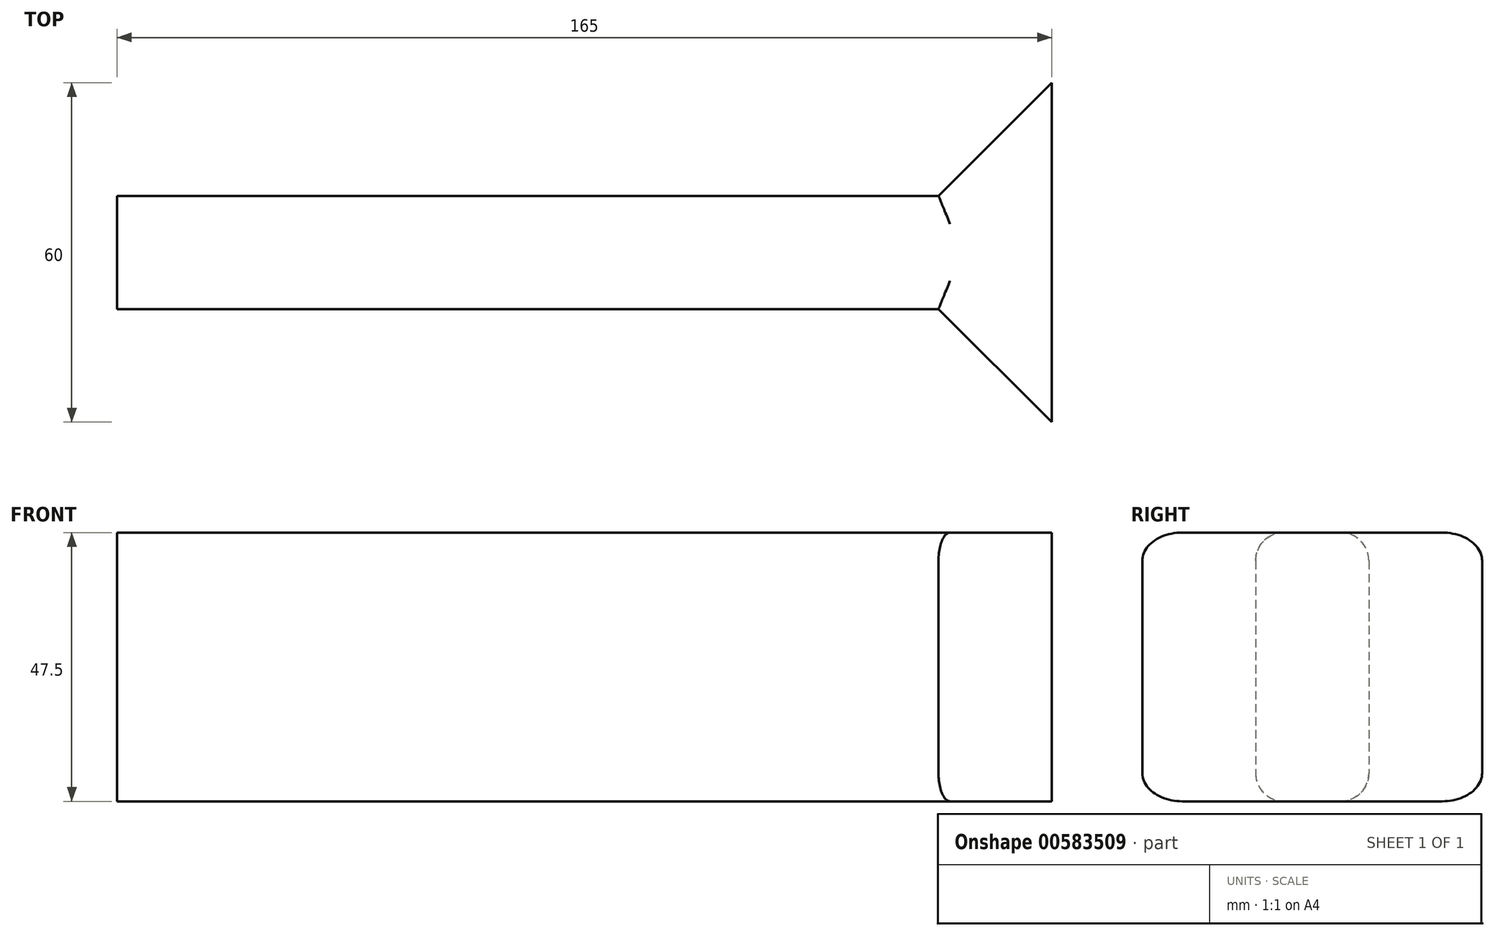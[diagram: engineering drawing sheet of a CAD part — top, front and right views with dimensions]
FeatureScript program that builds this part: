
annotation { "Feature Type Name" : "Feature", "Feature Type Description" : "" }
export const myFeature = defineFeature(function(context is Context, id is Id, definition is map)
    precondition{}
    {
        {
            var Q0;
            Q0=qCreatedBy(makeId("Top.planeOp"),FACE);
            var sketch = newSketch(context, id + "F0", { "sketchPlane" : qUnion([Q0])});
            skLineSegment(sketch, "E0.bottom", {"start": v(-165, -20) * mm, "end": v(-20, -20) * mm});
            skLineSegment(sketch, "E0.top", {"start": v(-165, 0) * mm, "end": v(-20, 0) * mm});
            skLineSegment(sketch, "E0.left", {"start": v(-165, -20) * mm, "end": v(-165, 0) * mm});
            skLineSegment(sketch, "E0.right", {"start": v(0, -20) * mm, "end": v(0, 0) * mm});
            skLineSegment(sketch, "E1.left", {"start": v(0, 0) * mm, "end": v(0, 20) * mm});
            skLineSegment(sketch, "E2", {"start": v(0, -20) * mm, "end": v(0, -40) * mm});
            skLineSegment(sketch, "E3", {"start": v(-20, -20) * mm, "end": v(0, -40) * mm});
            skLineSegment(sketch, "E4", {"start": v(-20, 0) * mm, "end": v(0, 20) * mm});
            skSolve(sketch);
        }
        {
            var Q0;
            Q0 = qSketchRegion(id + "F0", true);
            extrude(context, id + "F1", {"entities" : qUnion([Q0]), "depth" : 47.5 * mm, "offsetDistance" : 25 * mm});
        }
        {
            var Q0;
            Q0=makeQuery(id+"F1.opExtrude","CAP_EDGE",EDGE,{"disambiguationData":[OSD([sQuery(id+"F0.wireOp",EDGE,"E0.bottom")])],"isStart":false});
            var Q1;
            Q1=makeQuery(id+"F1.opExtrude","CAP_EDGE",EDGE,{"disambiguationData":[OSD([sQuery(id+"F0.wireOp",EDGE,"E0.top")])],"isStart":false});
            var Q2;
            Q2=makeQuery(id+"F1.opExtrude","CAP_EDGE",EDGE,{"disambiguationData":[OSD([sQuery(id+"F0.wireOp",EDGE,"E0.top")])],"isStart":true});
            var Q3;
            Q3=makeQuery(id+"F1.opExtrude","CAP_EDGE",EDGE,{"disambiguationData":[OSD([sQuery(id+"F0.wireOp",EDGE,"E0.bottom")])],"isStart":true});
            var Q4;
            Q4=makeQuery(id+"F1.opExtrude","CAP_EDGE",EDGE,{"disambiguationData":[OSD([sQuery(id+"F0.wireOp",EDGE,"E4")])],"isStart":true});
            var Q5;
            Q5=makeQuery(id+"F1.opExtrude","CAP_EDGE",EDGE,{"disambiguationData":[OSD([sQuery(id+"F0.wireOp",EDGE,"E4")])],"isStart":false});
            var Q6;
            Q6=makeQuery(id+"F1.opExtrude","CAP_EDGE",EDGE,{"disambiguationData":[OSD([sQuery(id+"F0.wireOp",EDGE,"E3")])],"isStart":false});
            var Q7;
            Q7=makeQuery(id+"F1.opExtrude","CAP_EDGE",EDGE,{"disambiguationData":[OSD([sQuery(id+"F0.wireOp",EDGE,"E3")])],"isStart":true});
            fillet(context, id + "F2", {"entities" : qUnion([Q0, Q1, Q2, Q3, Q4, Q5, Q6, Q7]), "radius" : 5 * mm, "tangentPropagation" : true, "allowEdgeOverflow" : false});
        }
    });
